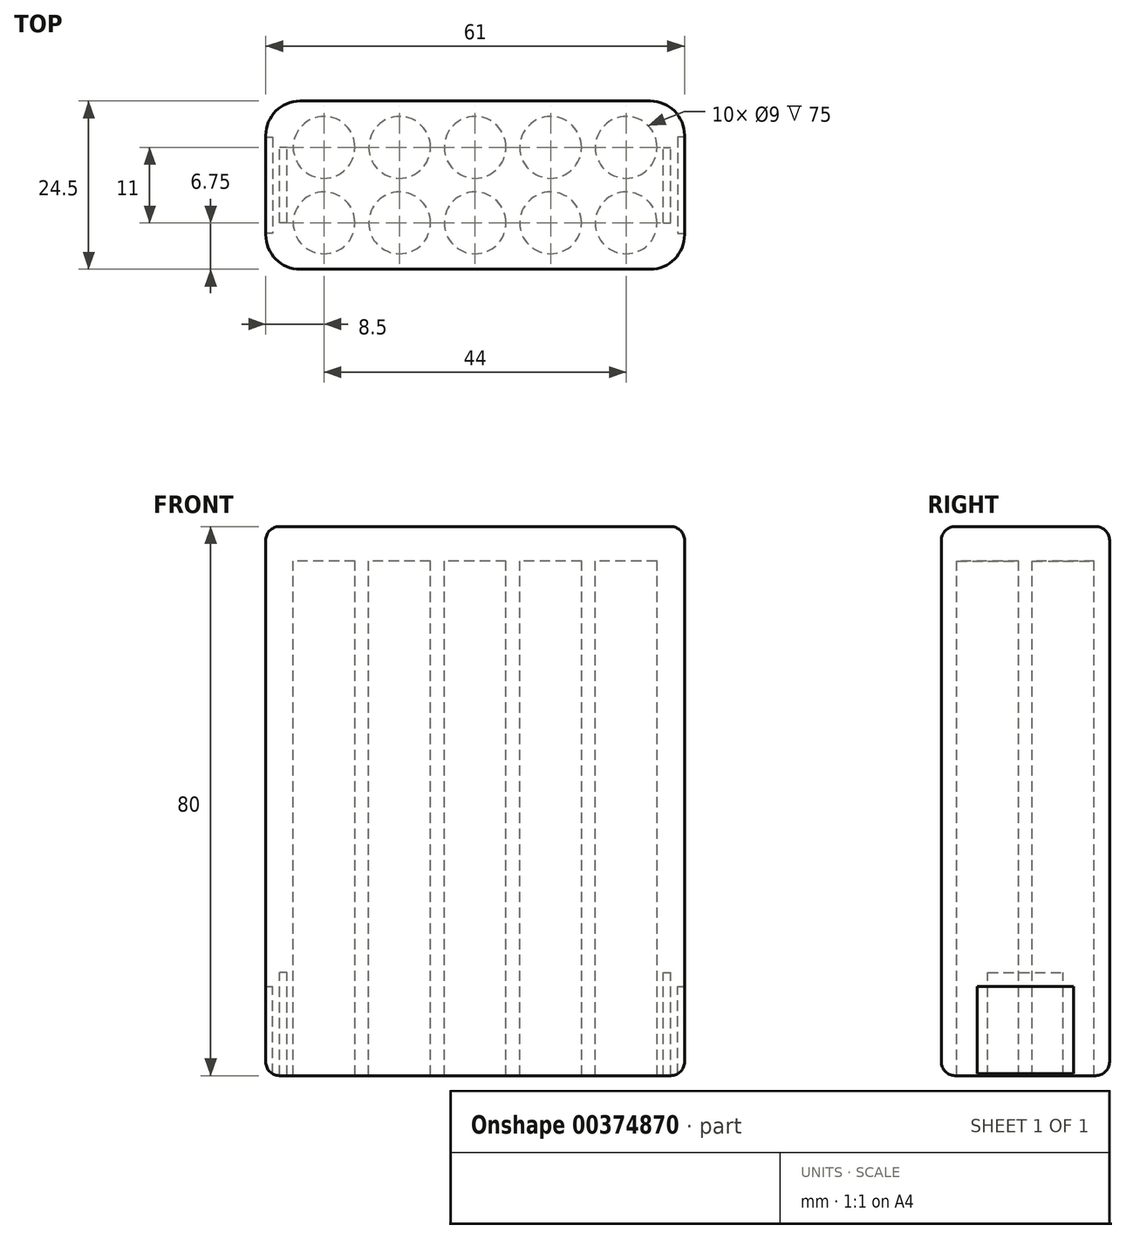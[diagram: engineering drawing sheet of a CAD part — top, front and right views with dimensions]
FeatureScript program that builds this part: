
annotation { "Feature Type Name" : "Feature", "Feature Type Description" : "" }
export const myFeature = defineFeature(function(context is Context, id is Id, definition is map)
    precondition{}
    {
        {
            var Q0;
            Q0=qCreatedBy(makeId("Top.planeOp"),FACE);
            var sketch = newSketch(context, id + "F0", { "sketchPlane" : qUnion([Q0])});
            skCircle(sketch, "E0", {"center": v(-22, -5.5) * mm, "radius": 4.5 * mm});
            skCircle(sketch, "E1.0.1.0", {"center": v(-22, 5.5) * mm, "radius": 4.5 * mm});
            skCircle(sketch, "E1.1.0.0", {"center": v(-11, -5.5) * mm, "radius": 4.5 * mm});
            skCircle(sketch, "E1.1.1.0", {"center": v(-11, 5.5) * mm, "radius": 4.5 * mm});
            skCircle(sketch, "E1.2.0.0", {"center": v(0, -5.5) * mm, "radius": 4.5 * mm});
            skCircle(sketch, "E1.2.1.0", {"center": v(0, 5.5) * mm, "radius": 4.5 * mm});
            skCircle(sketch, "E1.3.0.0", {"center": v(11, -5.5) * mm, "radius": 4.5 * mm});
            skCircle(sketch, "E1.3.1.0", {"center": v(11, 5.5) * mm, "radius": 4.5 * mm});
            skCircle(sketch, "E1.4.0.0", {"center": v(22, -5.5) * mm, "radius": 4.5 * mm});
            skCircle(sketch, "E1.4.1.0", {"center": v(22, 5.5) * mm, "radius": 4.5 * mm});
            skLineSegment(sketch, "E1.direction1", {"start": v(-22, -5.5) * mm, "end": v(-11, -5.5) * mm, "construction": true});
            skLineSegment(sketch, "E1.direction2", {"start": v(-22, -5.5) * mm, "end": v(-22, 5.5) * mm, "construction": true});
            skPoint(sketch, "E2", {"position": v(0, 0) * mm});
            skLineSegment(sketch, "E3.bottom", {"start": v(30.5, 12.25) * mm, "end": v(-30.5, 12.25) * mm});
            skLineSegment(sketch, "E3.top", {"start": v(30.5, -12.25) * mm, "end": v(-30.5, -12.25) * mm});
            skLineSegment(sketch, "E3.left", {"start": v(30.5, 12.25) * mm, "end": v(30.5, -12.25) * mm});
            skLineSegment(sketch, "E3.right", {"start": v(-30.5, 12.25) * mm, "end": v(-30.5, -12.25) * mm});
            skLineSegment(sketch, "E4.bottom", {"start": v(-27.4, -5.5) * mm, "end": v(-28.5, -5.5) * mm});
            skLineSegment(sketch, "E4.top", {"start": v(-27.4, 5.5) * mm, "end": v(-28.5, 5.5) * mm});
            skLineSegment(sketch, "E4.left", {"start": v(-27.4, -5.5) * mm, "end": v(-27.4, 5.5) * mm});
            skLineSegment(sketch, "E4.right", {"start": v(-28.5, -5.5) * mm, "end": v(-28.5, 5.5) * mm});
            skPoint(sketch, "E4.middle", {"position": v(-27.95, 0) * mm});
            skLineSegment(sketch, "E5.MirrorCS", {"start": v(28.5, -5.5) * mm, "end": v(28.5, 5.5) * mm});
            skLineSegment(sketch, "E6.MirrorCS", {"start": v(27.4, -5.5) * mm, "end": v(27.4, 5.5) * mm});
            skLineSegment(sketch, "E7.MirrorCS", {"start": v(27.4, 5.5) * mm, "end": v(28.5, 5.5) * mm});
            skLineSegment(sketch, "E8.MirrorCS", {"start": v(27.4, -5.5) * mm, "end": v(28.5, -5.5) * mm});
            skPoint(sketch, "E9", {"position": v(-30.5, 7) * mm});
            skPoint(sketch, "E10", {"position": v(-30.5, -7) * mm});
            skPoint(sketch, "E11", {"position": v(-29.5, -7) * mm});
            skPoint(sketch, "E12", {"position": v(-29.5, 7) * mm});
            skLineSegment(sketch, "E13", {"start": v(-30.5, 7) * mm, "end": v(-29.5, 7) * mm});
            skLineSegment(sketch, "E14", {"start": v(-29.5, 7) * mm, "end": v(-29.5, -7) * mm});
            skLineSegment(sketch, "E15", {"start": v(-29.5, -7) * mm, "end": v(-30.5, -7) * mm});
            skPoint(sketch, "E16", {"position": v(-29.5, 0) * mm});
            skLineSegment(sketch, "E17.MirrorCS", {"start": v(30.5, 7) * mm, "end": v(29.5, 7) * mm});
            skLineSegment(sketch, "E18.MirrorCS", {"start": v(29.5, -7) * mm, "end": v(30.5, -7) * mm});
            skLineSegment(sketch, "E19.MirrorCS", {"start": v(29.5, 7) * mm, "end": v(29.5, -7) * mm});
            skSolve(sketch);
        }
        {
            var Q0;
            {var subQ0=sQuery(id+"F0.wireOp",EDGE,"E17.MirrorCS");Q0=makeQuery(id+"F0.imprint","IMPRINT",FACE,{"disambiguationData":[TD([[makeQuery(id+"F0.imprint","IMPRINT",EDGE,{"derivedFrom":subQ0}),1.0]])]});}
            var Q1;
            {var subQ0=sQuery(id+"F0.wireOp",EDGE,"E13");Q1=makeQuery(id+"F0.imprint","IMPRINT",FACE,{"disambiguationData":[TD([[makeQuery(id+"F0.imprint","IMPRINT",EDGE,{"derivedFrom":subQ0}),-1.0]])]});}
            var Q2;
            Q2=makeQuery(id+"F0.imprint","IMPRINT",FACE,{"disambiguationData":[TD([[makeQuery(id+"F0.imprint","IMPRINT",EDGE,{"derivedFrom":sQuery(id+"F0.wireOp",EDGE,"E0")}),-1.0]])]});
            var Q3;
            Q3=makeQuery(id+"F0.imprint","IMPRINT",FACE,{"disambiguationData":[TD([[makeQuery(id+"F0.imprint","IMPRINT",EDGE,{"derivedFrom":sQuery(id+"F0.wireOp",EDGE,"E4.bottom")}),-1.0]])]});
            var Q4;
            Q4=makeQuery(id+"F0.imprint","IMPRINT",FACE,{"disambiguationData":[TD([[makeQuery(id+"F0.imprint","IMPRINT",EDGE,{"derivedFrom":sQuery(id+"F0.wireOp",EDGE,"E5.MirrorCS")}),1.0]])]});
            var Q5;
            Q5=makeQuery(id+"F0.imprint","IMPRINT",FACE,{"disambiguationData":[TD([[makeQuery(id+"F0.imprint","IMPRINT",EDGE,{"derivedFrom":sQuery(id+"F0.wireOp",EDGE,"E1.4.1.0")}),1.0]])]});
            var Q6;
            Q6=makeQuery(id+"F0.imprint","IMPRINT",FACE,{"disambiguationData":[TD([[makeQuery(id+"F0.imprint","IMPRINT",EDGE,{"derivedFrom":sQuery(id+"F0.wireOp",EDGE,"E1.4.0.0")}),1.0]])]});
            var Q7;
            Q7=makeQuery(id+"F0.imprint","IMPRINT",FACE,{"disambiguationData":[TD([[makeQuery(id+"F0.imprint","IMPRINT",EDGE,{"derivedFrom":sQuery(id+"F0.wireOp",EDGE,"E1.3.0.0")}),1.0]])]});
            var Q8;
            Q8=makeQuery(id+"F0.imprint","IMPRINT",FACE,{"disambiguationData":[TD([[makeQuery(id+"F0.imprint","IMPRINT",EDGE,{"derivedFrom":sQuery(id+"F0.wireOp",EDGE,"E1.3.1.0")}),1.0]])]});
            var Q9;
            Q9=makeQuery(id+"F0.imprint","IMPRINT",FACE,{"disambiguationData":[TD([[makeQuery(id+"F0.imprint","IMPRINT",EDGE,{"derivedFrom":sQuery(id+"F0.wireOp",EDGE,"E1.2.1.0")}),1.0]])]});
            var Q10;
            Q10=makeQuery(id+"F0.imprint","IMPRINT",FACE,{"disambiguationData":[TD([[makeQuery(id+"F0.imprint","IMPRINT",EDGE,{"derivedFrom":sQuery(id+"F0.wireOp",EDGE,"E1.2.0.0")}),1.0]])]});
            var Q11;
            Q11=makeQuery(id+"F0.imprint","IMPRINT",FACE,{"disambiguationData":[TD([[makeQuery(id+"F0.imprint","IMPRINT",EDGE,{"derivedFrom":sQuery(id+"F0.wireOp",EDGE,"E1.1.0.0")}),1.0]])]});
            var Q12;
            Q12=makeQuery(id+"F0.imprint","IMPRINT",FACE,{"disambiguationData":[TD([[makeQuery(id+"F0.imprint","IMPRINT",EDGE,{"derivedFrom":sQuery(id+"F0.wireOp",EDGE,"E1.1.1.0")}),1.0]])]});
            var Q13;
            Q13=makeQuery(id+"F0.imprint","IMPRINT",FACE,{"disambiguationData":[TD([[makeQuery(id+"F0.imprint","IMPRINT",EDGE,{"derivedFrom":sQuery(id+"F0.wireOp",EDGE,"E1.0.1.0")}),1.0]])]});
            var Q14;
            Q14=makeQuery(id+"F0.imprint","IMPRINT",FACE,{"disambiguationData":[TD([[makeQuery(id+"F0.imprint","IMPRINT",EDGE,{"derivedFrom":sQuery(id+"F0.wireOp",EDGE,"E0")}),1.0]])]});
            extrude(context, id + "F1", {"entities" : qUnion([Q0, Q1, Q2, Q3, Q4, Q5, Q6, Q7, Q8, Q9, Q10, Q11, Q12, Q13, Q14]), "depth" : 5 * mm});
        }
        {
            var Q0;
            Q0=makeQuery(id+"F0.imprint","IMPRINT",FACE,{"disambiguationData":[TD([[makeQuery(id+"F0.imprint","IMPRINT",EDGE,{"derivedFrom":sQuery(id+"F0.wireOp",EDGE,"E0")}),-1.0]])]});
            extrude(context, id + "F2", {"entities" : qUnion([Q0]), "operationType" : NewBodyOperationType.ADD, "oppositeDirection" : true, "depth" : 75 * mm});
        }
        {
            var Q0;
            {var subQ0=sQuery(id+"F0.wireOp",EDGE,"E3.left");var subQ1=sQuery(id+"F0.wireOp",EDGE,"E3.bottom");Q0=makeQuery(id+"F2.boolean.opBoolean","MERGE",EDGE,{"derivedFrom":[makeQuery(id+"F1.opExtrude","SWEPT_EDGE",EDGE,{"disambiguationData":[OSD([subQ1,subQ0])]}),makeQuery(id+"F2.opExtrude","SWEPT_EDGE",EDGE,{"disambiguationData":[OSD([subQ1,subQ0])]})]});}
            var Q1;
            {var subQ0=sQuery(id+"F0.wireOp",EDGE,"E3.left");var subQ1=sQuery(id+"F0.wireOp",EDGE,"E3.top");Q1=makeQuery(id+"F2.boolean.opBoolean","MERGE",EDGE,{"derivedFrom":[makeQuery(id+"F1.opExtrude","SWEPT_EDGE",EDGE,{"disambiguationData":[OSD([subQ1,subQ0])]}),makeQuery(id+"F2.opExtrude","SWEPT_EDGE",EDGE,{"disambiguationData":[OSD([subQ1,subQ0])]})]});}
            var Q2;
            {var subQ0=sQuery(id+"F0.wireOp",EDGE,"E3.right");var subQ1=sQuery(id+"F0.wireOp",EDGE,"E3.top");Q2=makeQuery(id+"F2.boolean.opBoolean","MERGE",EDGE,{"derivedFrom":[makeQuery(id+"F1.opExtrude","SWEPT_EDGE",EDGE,{"disambiguationData":[OSD([subQ1,subQ0])]}),makeQuery(id+"F2.opExtrude","SWEPT_EDGE",EDGE,{"disambiguationData":[OSD([subQ1,subQ0])]})]});}
            var Q3;
            {var subQ0=sQuery(id+"F0.wireOp",EDGE,"E3.right");var subQ1=sQuery(id+"F0.wireOp",EDGE,"E3.bottom");Q3=makeQuery(id+"F2.boolean.opBoolean","MERGE",EDGE,{"derivedFrom":[makeQuery(id+"F1.opExtrude","SWEPT_EDGE",EDGE,{"disambiguationData":[OSD([subQ1,subQ0])]}),makeQuery(id+"F2.opExtrude","SWEPT_EDGE",EDGE,{"disambiguationData":[OSD([subQ1,subQ0])]})]});}
            fillet(context, id + "F3", {"entities" : qUnion([Q0, Q1, Q2, Q3]), "radius" : 5 * mm, "tangentPropagation" : true, "allowEdgeOverflow" : false});
        }
        {
            var Q0;
            Q0=makeQuery(id+"F2.opExtrude","CAP_EDGE",EDGE,{"disambiguationData":[OSD([sQuery(id+"F0.wireOp",EDGE,"E3.bottom")])],"isStart":false});
            var Q1;
            Q1=makeQuery(id+"F2.opExtrude","CAP_EDGE",EDGE,{"disambiguationData":[OSD([sQuery(id+"F0.wireOp",EDGE,"E3.top")])],"isStart":false});
            fillet(context, id + "F4", {"entities" : qUnion([Q0, Q1]), "radius" : 2 * mm, "tangentPropagation" : true, "allowEdgeOverflow" : false});
        }
        {
            var Q0;
            {var subQ0=sQuery(id+"F0.wireOp",EDGE,"E13");Q0=makeQuery(id+"F0.imprint","IMPRINT",FACE,{"disambiguationData":[TD([[makeQuery(id+"F0.imprint","IMPRINT",EDGE,{"derivedFrom":subQ0}),-1.0]])]});}
            extrude(context, id + "F5", {"entities" : qUnion([Q0]), "operationType" : NewBodyOperationType.ADD, "oppositeDirection" : true, "depth" : 62 * mm});
        }
        {
            var Q0;
            {var subQ0=sQuery(id+"F0.wireOp",EDGE,"E17.MirrorCS");Q0=makeQuery(id+"F0.imprint","IMPRINT",FACE,{"disambiguationData":[TD([[makeQuery(id+"F0.imprint","IMPRINT",EDGE,{"derivedFrom":subQ0}),1.0]])]});}
            extrude(context, id + "F6", {"entities" : qUnion([Q0]), "operationType" : NewBodyOperationType.ADD, "oppositeDirection" : true, "depth" : 62 * mm});
        }
        {
            var Q0;
            Q0=makeQuery(id+"F1.opExtrude","CAP_FACE",FACE,{"disambiguationData":[OSD([sQuery(id+"F0.wireOp",EDGE,"E3.bottom"),sQuery(id+"F0.wireOp",EDGE,"E3.top"),sQuery(id+"F0.wireOp",EDGE,"E3.left"),sQuery(id+"F0.wireOp",EDGE,"E3.right")])],"isStart":false});
            fillet(context, id + "F7", {"entities" : qUnion([Q0]), "radius" : 2 * mm, "tangentPropagation" : true, "allowEdgeOverflow" : false});
        }
        {
            var Q0;
            Q0=makeQuery(id+"F0.imprint","IMPRINT",FACE,{"disambiguationData":[TD([[makeQuery(id+"F0.imprint","IMPRINT",EDGE,{"derivedFrom":sQuery(id+"F0.wireOp",EDGE,"E4.bottom")}),-1.0]])]});
            var Q1;
            Q1=makeQuery(id+"F0.imprint","IMPRINT",FACE,{"disambiguationData":[TD([[makeQuery(id+"F0.imprint","IMPRINT",EDGE,{"derivedFrom":sQuery(id+"F0.wireOp",EDGE,"E5.MirrorCS")}),1.0]])]});
            extrude(context, id + "F8", {"entities" : qUnion([Q0, Q1]), "operationType" : NewBodyOperationType.ADD, "oppositeDirection" : true, "depth" : 60 * mm, "offsetDistance" : 25 * mm});
        }
    });
